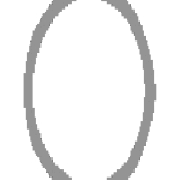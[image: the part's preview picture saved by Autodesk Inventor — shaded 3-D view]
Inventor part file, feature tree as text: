
AUTODESK INVENTOR PART (.ipt)
format: ipt  version: 2021 (Build 250183000, 183)  size: 111,616 bytes
history: native  units: in
note: dims shown in document units (in); Inventor stores cm internally (conversion verified against a paired STEP export)
features: other x4, sketch x3, plane x1
ambient origin geometry x8: Origin, YZ Plane, XZ Plane, XY Plane, X Axis, Y Axis, Z Axis, Center Point
bodies: Solid1 (feature_tree), Body (feature_tree)
feature tree (8):
  other  "Driven Length"
  other  "Frame Generator"
  other  "Start Plane"
  other  "End Plane"
  sketch  "Sketch"  dims[d2=22.3842in d4=-0.0in d5=22.3842in d6=0.12in d7=0.0in d8=90.0deg d9=22.3842in]
  sketch  "Sketch2"  dims[d0=1.0in]
  plane  "Work Plane3"
  sketch  "Sketch3"  dims[d1=0.065in]
